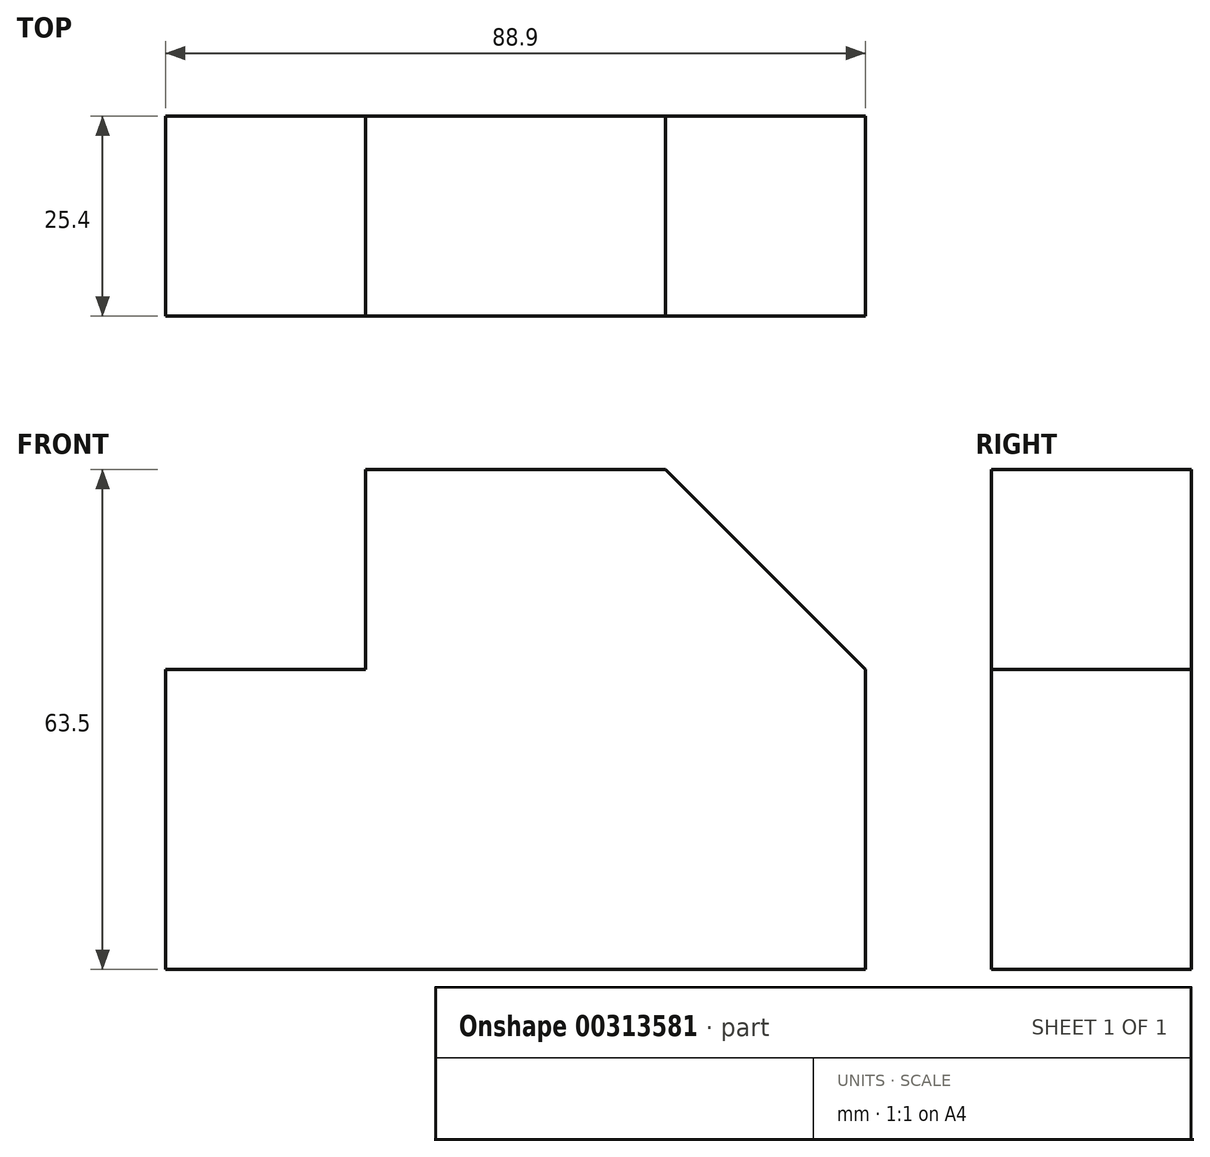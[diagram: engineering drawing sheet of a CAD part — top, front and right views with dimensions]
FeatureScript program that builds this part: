
annotation { "Feature Type Name" : "Feature", "Feature Type Description" : "" }
export const myFeature = defineFeature(function(context is Context, id is Id, definition is map)
    precondition{}
    {
        {
            var Q0;
            Q0=qCreatedBy(makeId("Front.planeOp"),FACE);
            var sketch = newSketch(context, id + "F0", { "sketchPlane" : qUnion([Q0])});
            skLineSegment(sketch, "E0", {"start": v(-31.85, -47.5) * mm, "end": v(57.05, -47.5) * mm});
            skLineSegment(sketch, "E1", {"start": v(57.05, -47.5) * mm, "end": v(57.05, -9.4) * mm});
            skLineSegment(sketch, "E2", {"start": v(57.05, -9.4) * mm, "end": v(31.65, 16) * mm});
            skLineSegment(sketch, "E3", {"start": v(31.65, 16) * mm, "end": v(-6.45, 16) * mm});
            skLineSegment(sketch, "E4", {"start": v(-6.45, 16) * mm, "end": v(-6.45, -9.4) * mm});
            skLineSegment(sketch, "E5", {"start": v(-6.45, -9.4) * mm, "end": v(-31.85, -9.4) * mm});
            skLineSegment(sketch, "E6", {"start": v(-31.85, -9.4) * mm, "end": v(-31.85, -47.5) * mm});
            skSolve(sketch);
        }
        {
            var Q0;
            Q0=makeQuery(id+"F0.imprint","IMPRINT",FACE,{"disambiguationData":[TD([[makeQuery(id+"F0.imprint","IMPRINT",EDGE,{"derivedFrom":sQuery(id+"F0.wireOp",EDGE,"E0")}),1.0]])]});
            extrude(context, id + "F1", {"entities" : qUnion([Q0]), "depth" : 25.4 * mm});
        }
    });
